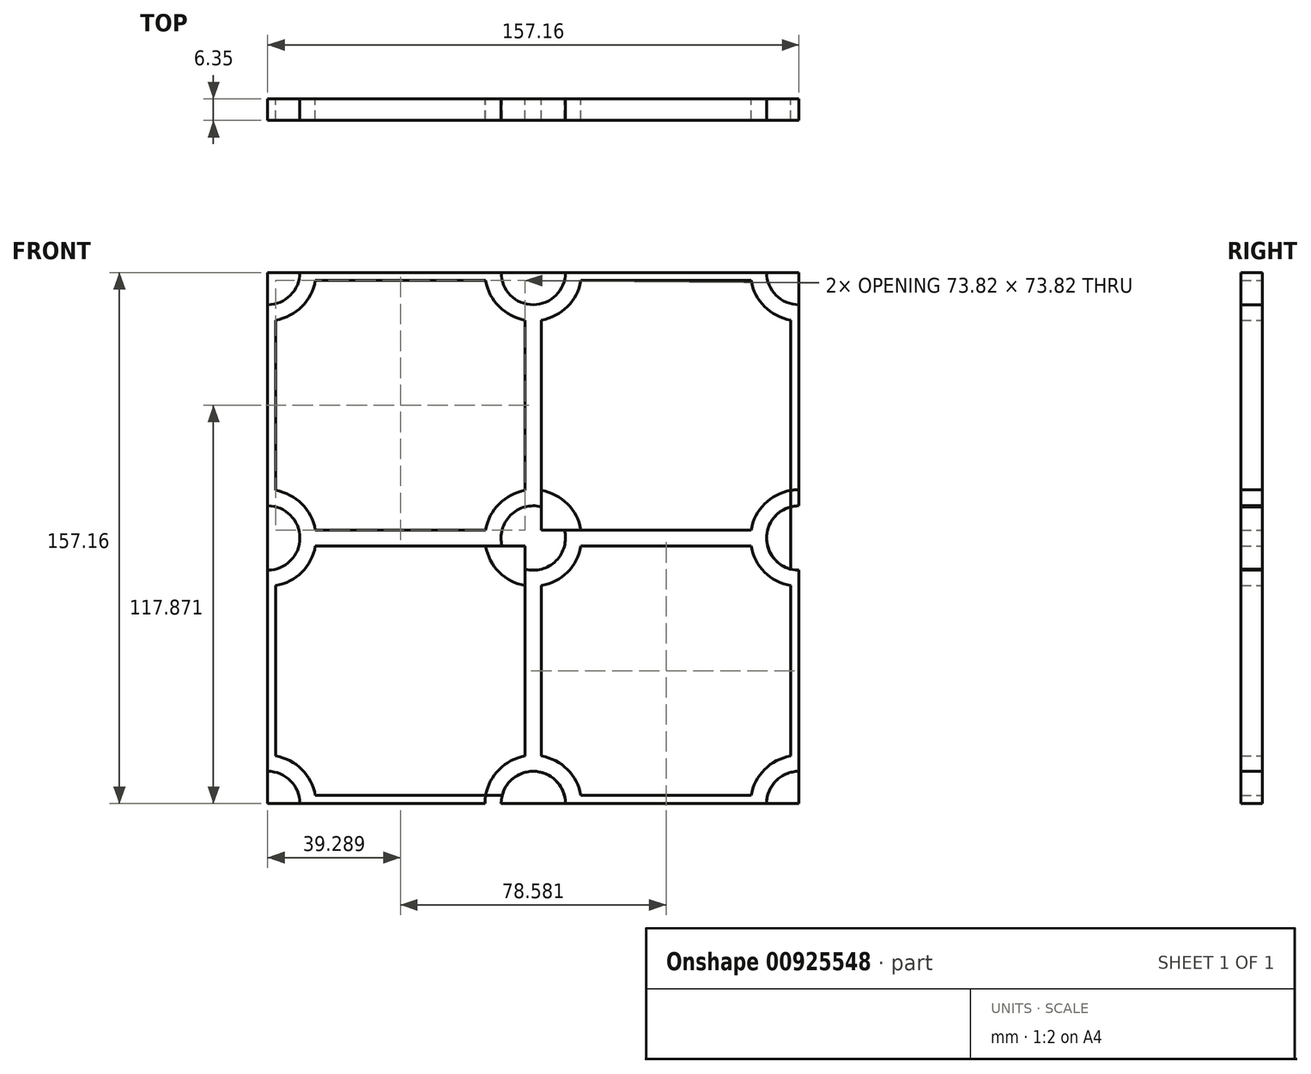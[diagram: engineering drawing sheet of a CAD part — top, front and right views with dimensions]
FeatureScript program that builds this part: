
annotation { "Feature Type Name" : "Feature", "Feature Type Description" : "" }
export const myFeature = defineFeature(function(context is Context, id is Id, definition is map)
    precondition{}
    {
        {
            var Q0;
            Q0=qCreatedBy(makeId("Front.planeOp"),FACE);
            var sketch = newSketch(context, id + "F0", { "sketchPlane" : qUnion([Q0])});
            skLineSegment(sketch, "E0.bottom", {"start": v(76.2, -76.2) * mm, "end": v(-76.2, -76.2) * mm});
            skLineSegment(sketch, "E0.top", {"start": v(76.2, 76.2) * mm, "end": v(-76.2, 76.2) * mm});
            skLineSegment(sketch, "E0.left", {"start": v(76.2, -76.2) * mm, "end": v(76.2, 76.2) * mm});
            skLineSegment(sketch, "E0.right", {"start": v(-76.2, -76.2) * mm, "end": v(-76.2, 76.2) * mm});
            skPoint(sketch, "E0.middle", {"position": v(0, 0) * mm});
            skSolve(sketch);
        }
        {
            var Q0;
            Q0=makeQuery(id+"F0.imprint","IMPRINT",FACE,{"disambiguationData":[TD([[makeQuery(id+"F0.imprint","IMPRINT",EDGE,{"derivedFrom":sQuery(id+"F0.wireOp",EDGE,"E0.bottom")}),-1.0]])]});
            var sketch = newSketch(context, id + "F1", { "sketchPlane" : qUnion([Q0])});
            skLineSegment(sketch, "E1.bottom", {"start": v(78.58, -78.58) * mm, "end": v(-78.58, -78.58) * mm});
            skLineSegment(sketch, "E1.top", {"start": v(78.58, 78.58) * mm, "end": v(-78.58, 78.58) * mm});
            skLineSegment(sketch, "E1.left", {"start": v(78.58, -78.58) * mm, "end": v(78.58, 78.58) * mm});
            skLineSegment(sketch, "E1.right", {"start": v(-78.58, -78.58) * mm, "end": v(-78.58, 78.58) * mm});
            skPoint(sketch, "E1.middle", {"position": v(0, 0) * mm});
            skLineSegment(sketch, "E2", {"start": v(-78.58, 0) * mm, "end": v(78.58, 0) * mm, "construction": true});
            skLineSegment(sketch, "E3", {"start": v(0, 78.58) * mm, "end": v(0, -78.58) * mm, "construction": true});
            skLineSegment(sketch, "E4.bottom", {"start": v(76.2, -76.2) * mm, "end": v(-76.2, -76.2) * mm});
            skLineSegment(sketch, "E4.top", {"start": v(76.2, 76.2) * mm, "end": v(-76.2, 76.2) * mm});
            skLineSegment(sketch, "E4.left", {"start": v(76.2, -76.2) * mm, "end": v(76.2, 76.2) * mm});
            skLineSegment(sketch, "E4.right", {"start": v(-76.2, -76.2) * mm, "end": v(-76.2, 76.2) * mm});
            skCircle(sketch, "E5", {"center": v(-78.58, 78.58) * mm, "radius": 9.53 * mm});
            skCircle(sketch, "E6", {"center": v(-78.58, 78.58) * mm, "radius": 14.29 * mm});
            skCircle(sketch, "E7.0.1.0", {"center": v(-78.58, 0) * mm, "radius": 14.29 * mm});
            skCircle(sketch, "E7.0.1.1", {"center": v(-78.58, 0) * mm, "radius": 9.53 * mm});
            skCircle(sketch, "E7.0.2.0", {"center": v(-78.58, -78.58) * mm, "radius": 14.29 * mm});
            skCircle(sketch, "E7.0.2.1", {"center": v(-78.58, -78.58) * mm, "radius": 9.53 * mm});
            skCircle(sketch, "E7.1.0.0", {"center": v(0, 78.58) * mm, "radius": 14.29 * mm});
            skCircle(sketch, "E7.1.0.1", {"center": v(0, 78.58) * mm, "radius": 9.53 * mm});
            skCircle(sketch, "E7.1.1.0", {"center": v(0, 0) * mm, "radius": 14.29 * mm});
            skCircle(sketch, "E7.1.1.1", {"center": v(0, 0) * mm, "radius": 9.53 * mm});
            skCircle(sketch, "E7.1.2.0", {"center": v(0, -78.58) * mm, "radius": 14.29 * mm});
            skCircle(sketch, "E7.1.2.1", {"center": v(0, -78.58) * mm, "radius": 9.53 * mm});
            skCircle(sketch, "E7.2.0.0", {"center": v(78.58, 78.58) * mm, "radius": 14.29 * mm});
            skCircle(sketch, "E7.2.0.1", {"center": v(78.58, 78.58) * mm, "radius": 9.53 * mm});
            skCircle(sketch, "E7.2.1.0", {"center": v(78.58, 0) * mm, "radius": 14.29 * mm});
            skCircle(sketch, "E7.2.1.1", {"center": v(78.58, 0) * mm, "radius": 9.53 * mm});
            skCircle(sketch, "E7.2.2.0", {"center": v(78.58, -78.58) * mm, "radius": 14.29 * mm});
            skCircle(sketch, "E7.2.2.1", {"center": v(78.58, -78.58) * mm, "radius": 9.53 * mm});
            skLineSegment(sketch, "E7.direction1", {"start": v(-78.58, 78.58) * mm, "end": v(0, 78.58) * mm, "construction": true});
            skLineSegment(sketch, "E7.direction2", {"start": v(-78.58, 78.58) * mm, "end": v(-78.58, 0) * mm, "construction": true});
            skLineSegment(sketch, "E8.0", {"start": v(-2.38, 76.2) * mm, "end": v(-2.38, -76.2) * mm});
            skLineSegment(sketch, "E9.0", {"start": v(2.38, 76.2) * mm, "end": v(2.38, -76.2) * mm});
            skLineSegment(sketch, "E10.0", {"start": v(-76.2, -2.38) * mm, "end": v(76.2, -2.38) * mm});
            skLineSegment(sketch, "E11.0", {"start": v(-76.2, 2.38) * mm, "end": v(76.2, 2.38) * mm});
            skSolve(sketch);
        }
        {
            var Q0;
            {var subQ7=sQuery(id+"F1.wireOp",EDGE,"E7.1.0.0");var subQ8=sQuery(id+"F1.wireOp",EDGE,"E4.top");var subQ9=makeQuery(id+"F1.imprint","INTERSECT",VERTEX,{"disambiguationData":[OD(1.0)],"derivedFrom":[subQ8,subQ7]});Q0=makeQuery(id+"F1.imprint","IMPRINT",FACE,{"disambiguationData":[TD([[makeQuery(id+"F1.imprint","IMPRINT",EDGE,{"disambiguationData":[TD([[subQ9,-1.0]])],"derivedFrom":subQ8}),1.0]])]});}
            var Q1;
            {var subQ6=sQuery(id+"F1.wireOp",EDGE,"E4.top");var subQ12=sQuery(id+"F1.wireOp",EDGE,"E7.2.0.0");var subQ14=makeQuery(id+"F1.imprint","INTERSECT",VERTEX,{"derivedFrom":[subQ6,subQ12]});Q1=makeQuery(id+"F1.imprint","IMPRINT",FACE,{"disambiguationData":[TD([[makeQuery(id+"F1.imprint","IMPRINT",EDGE,{"disambiguationData":[TD([[subQ14,-1.0]])],"derivedFrom":subQ6}),1.0]])]});}
            var Q2;
            {var subQ6=sQuery(id+"F1.wireOp",EDGE,"E4.bottom");var subQ9=sQuery(id+"F1.wireOp",EDGE,"E7.1.2.0");var subQ10=makeQuery(id+"F1.imprint","INTERSECT",VERTEX,{"disambiguationData":[OD(1.0)],"derivedFrom":[subQ6,subQ9]});Q2=makeQuery(id+"F1.imprint","IMPRINT",FACE,{"disambiguationData":[TD([[makeQuery(id+"F1.imprint","IMPRINT",EDGE,{"disambiguationData":[TD([[subQ10,-1.0]])],"derivedFrom":subQ6}),-1.0]])]});}
            var Q3;
            {var subQ1=sQuery(id+"F1.wireOp",EDGE,"E4.bottom");var subQ9=sQuery(id+"F1.wireOp",EDGE,"E7.2.2.0");var subQ14=makeQuery(id+"F1.imprint","INTERSECT",VERTEX,{"derivedFrom":[subQ1,subQ9]});Q3=makeQuery(id+"F1.imprint","IMPRINT",FACE,{"disambiguationData":[TD([[makeQuery(id+"F1.imprint","IMPRINT",EDGE,{"disambiguationData":[TD([[subQ14,-1.0]])],"derivedFrom":subQ1}),-1.0]])]});}
            extrude(context, id + "F2", {"entities" : qUnion([Q0, Q1, Q2, Q3]), "depth" : 6.35 * mm, "offsetDistance" : 30.48 * mm});
        }
        {
            var Q0;
            {var subQ0=sQuery(id+"F1.wireOp",EDGE,"E4.right");var subQ1=sQuery(id+"F1.wireOp",EDGE,"E4.top");var subQ2=makeQuery(id+"F1.imprint","INTERSECT",VERTEX,{"derivedFrom":[subQ1,subQ0]});Q0=makeQuery(id+"F1.imprint","IMPRINT",FACE,{"disambiguationData":[TD([[makeQuery(id+"F1.imprint","IMPRINT",EDGE,{"disambiguationData":[TD([[subQ2,1.0]])],"derivedFrom":subQ1}),1.0]])]});}
            var Q1;
            {var subQ5=sQuery(id+"F1.wireOp",EDGE,"E1.right");var subQ6=sQuery(id+"F1.wireOp",EDGE,"E1.top");var subQ7=makeQuery(id+"F1.imprint","INTERSECT",VERTEX,{"derivedFrom":[subQ6,subQ5]});Q1=makeQuery(id+"F1.imprint","IMPRINT",FACE,{"disambiguationData":[TD([[makeQuery(id+"F1.imprint","IMPRINT",EDGE,{"disambiguationData":[TD([[subQ7,1.0]])],"derivedFrom":subQ6}),1.0]])]});}
            var Q2;
            {var subQ3=sQuery(id+"F1.wireOp",EDGE,"E7.1.0.1");var subQ6=sQuery(id+"F1.wireOp",EDGE,"E1.top");var subQ7=makeQuery(id+"F1.imprint","INTERSECT",VERTEX,{"disambiguationData":[OD(0.0)],"derivedFrom":[subQ6,subQ3]});Q2=makeQuery(id+"F1.imprint","IMPRINT",FACE,{"disambiguationData":[TD([[makeQuery(id+"F1.imprint","IMPRINT",EDGE,{"disambiguationData":[TD([[subQ7,-1.0]])],"derivedFrom":subQ6}),1.0]])]});}
            var Q3;
            {var subQ0=sQuery(id+"F1.wireOp",EDGE,"E8.0");var subQ1=sQuery(id+"F1.wireOp",EDGE,"E4.top");var subQ2=makeQuery(id+"F1.imprint","INTERSECT",VERTEX,{"derivedFrom":[subQ1,subQ0]});Q3=makeQuery(id+"F1.imprint","IMPRINT",FACE,{"disambiguationData":[TD([[makeQuery(id+"F1.imprint","IMPRINT",EDGE,{"disambiguationData":[TD([[subQ2,-1.0]])],"derivedFrom":subQ1}),1.0]])]});}
            var Q4;
            {var subQ0=sQuery(id+"F1.wireOp",EDGE,"E8.0");var subQ1=sQuery(id+"F1.wireOp",EDGE,"E4.top");var subQ2=makeQuery(id+"F1.imprint","INTERSECT",VERTEX,{"derivedFrom":[subQ1,subQ0]});Q4=makeQuery(id+"F1.imprint","IMPRINT",FACE,{"disambiguationData":[TD([[makeQuery(id+"F1.imprint","IMPRINT",EDGE,{"disambiguationData":[TD([[subQ2,1.0]])],"derivedFrom":subQ1}),1.0]])]});}
            var Q5;
            {var subQ0=sQuery(id+"F1.wireOp",EDGE,"E9.0");var subQ1=sQuery(id+"F1.wireOp",EDGE,"E4.top");var subQ2=makeQuery(id+"F1.imprint","INTERSECT",VERTEX,{"derivedFrom":[subQ1,subQ0]});Q5=makeQuery(id+"F1.imprint","IMPRINT",FACE,{"disambiguationData":[TD([[makeQuery(id+"F1.imprint","IMPRINT",EDGE,{"disambiguationData":[TD([[subQ2,1.0]])],"derivedFrom":subQ1}),1.0]])]});}
            var Q6;
            {var subQ0=sQuery(id+"F1.wireOp",EDGE,"E4.left");var subQ1=sQuery(id+"F1.wireOp",EDGE,"E4.top");var subQ2=makeQuery(id+"F1.imprint","INTERSECT",VERTEX,{"derivedFrom":[subQ1,subQ0]});Q6=makeQuery(id+"F1.imprint","IMPRINT",FACE,{"disambiguationData":[TD([[makeQuery(id+"F1.imprint","IMPRINT",EDGE,{"disambiguationData":[TD([[subQ2,-1.0]])],"derivedFrom":subQ1}),1.0]])]});}
            var Q7;
            {var subQ6=sQuery(id+"F1.wireOp",EDGE,"E1.left");var subQ7=sQuery(id+"F1.wireOp",EDGE,"E1.top");var subQ8=makeQuery(id+"F1.imprint","INTERSECT",VERTEX,{"derivedFrom":[subQ7,subQ6]});Q7=makeQuery(id+"F1.imprint","IMPRINT",FACE,{"disambiguationData":[TD([[makeQuery(id+"F1.imprint","IMPRINT",EDGE,{"disambiguationData":[TD([[subQ8,-1.0]])],"derivedFrom":subQ7}),1.0]])]});}
            var Q8;
            {var subQ0=sQuery(id+"F1.wireOp",EDGE,"E11.0");var subQ1=sQuery(id+"F1.wireOp",EDGE,"E4.left");var subQ2=makeQuery(id+"F1.imprint","INTERSECT",VERTEX,{"derivedFrom":[subQ1,subQ0]});Q8=makeQuery(id+"F1.imprint","IMPRINT",FACE,{"disambiguationData":[TD([[makeQuery(id+"F1.imprint","IMPRINT",EDGE,{"disambiguationData":[TD([[subQ2,-1.0]])],"derivedFrom":subQ1}),1.0]])]});}
            var Q9;
            {var subQ2=sQuery(id+"F1.wireOp",EDGE,"E7.2.1.1");var subQ5=sQuery(id+"F1.wireOp",EDGE,"E1.left");var subQ8=makeQuery(id+"F1.imprint","INTERSECT",VERTEX,{"disambiguationData":[OD(0.0)],"derivedFrom":[subQ5,subQ2]});Q9=makeQuery(id+"F1.imprint","IMPRINT",FACE,{"disambiguationData":[TD([[makeQuery(id+"F1.imprint","IMPRINT",EDGE,{"disambiguationData":[TD([[subQ8,-1.0]])],"derivedFrom":subQ5}),1.0]])]});}
            var Q10;
            {var subQ0=sQuery(id+"F1.wireOp",EDGE,"E10.0");var subQ1=sQuery(id+"F1.wireOp",EDGE,"E4.left");var subQ2=makeQuery(id+"F1.imprint","INTERSECT",VERTEX,{"derivedFrom":[subQ1,subQ0]});Q10=makeQuery(id+"F1.imprint","IMPRINT",FACE,{"disambiguationData":[TD([[makeQuery(id+"F1.imprint","IMPRINT",EDGE,{"disambiguationData":[TD([[subQ2,-1.0]])],"derivedFrom":subQ1}),1.0]])]});}
            var Q11;
            {var subQ0=sQuery(id+"F1.wireOp",EDGE,"E10.0");var subQ1=sQuery(id+"F1.wireOp",EDGE,"E4.left");var subQ2=makeQuery(id+"F1.imprint","INTERSECT",VERTEX,{"derivedFrom":[subQ1,subQ0]});Q11=makeQuery(id+"F1.imprint","IMPRINT",FACE,{"disambiguationData":[TD([[makeQuery(id+"F1.imprint","IMPRINT",EDGE,{"disambiguationData":[TD([[subQ2,1.0]])],"derivedFrom":subQ1}),1.0]])]});}
            var Q12;
            {var subQ0=sQuery(id+"F1.wireOp",EDGE,"E4.left");var subQ1=sQuery(id+"F1.wireOp",EDGE,"E4.bottom");var subQ2=makeQuery(id+"F1.imprint","INTERSECT",VERTEX,{"derivedFrom":[subQ1,subQ0]});Q12=makeQuery(id+"F1.imprint","IMPRINT",FACE,{"disambiguationData":[TD([[makeQuery(id+"F1.imprint","IMPRINT",EDGE,{"disambiguationData":[TD([[subQ2,-1.0]])],"derivedFrom":subQ1}),-1.0]])]});}
            var Q13;
            {var subQ6=sQuery(id+"F1.wireOp",EDGE,"E1.left");var subQ7=sQuery(id+"F1.wireOp",EDGE,"E1.bottom");var subQ8=makeQuery(id+"F1.imprint","INTERSECT",VERTEX,{"derivedFrom":[subQ7,subQ6]});Q13=makeQuery(id+"F1.imprint","IMPRINT",FACE,{"disambiguationData":[TD([[makeQuery(id+"F1.imprint","IMPRINT",EDGE,{"disambiguationData":[TD([[subQ8,-1.0]])],"derivedFrom":subQ7}),-1.0]])]});}
            var Q14;
            {var subQ0=sQuery(id+"F1.wireOp",EDGE,"E9.0");var subQ1=sQuery(id+"F1.wireOp",EDGE,"E4.bottom");var subQ2=makeQuery(id+"F1.imprint","INTERSECT",VERTEX,{"derivedFrom":[subQ1,subQ0]});Q14=makeQuery(id+"F1.imprint","IMPRINT",FACE,{"disambiguationData":[TD([[makeQuery(id+"F1.imprint","IMPRINT",EDGE,{"disambiguationData":[TD([[subQ2,1.0]])],"derivedFrom":subQ1}),-1.0]])]});}
            var Q15;
            {var subQ0=sQuery(id+"F1.wireOp",EDGE,"E8.0");var subQ1=sQuery(id+"F1.wireOp",EDGE,"E4.bottom");var subQ2=makeQuery(id+"F1.imprint","INTERSECT",VERTEX,{"derivedFrom":[subQ1,subQ0]});Q15=makeQuery(id+"F1.imprint","IMPRINT",FACE,{"disambiguationData":[TD([[makeQuery(id+"F1.imprint","IMPRINT",EDGE,{"disambiguationData":[TD([[subQ2,-1.0]])],"derivedFrom":subQ1}),-1.0]])]});}
            var Q16;
            {var subQ2=sQuery(id+"F1.wireOp",EDGE,"E7.1.2.1");var subQ6=sQuery(id+"F1.wireOp",EDGE,"E1.bottom");var subQ7=makeQuery(id+"F1.imprint","INTERSECT",VERTEX,{"disambiguationData":[OD(0.0)],"derivedFrom":[subQ6,subQ2]});Q16=makeQuery(id+"F1.imprint","IMPRINT",FACE,{"disambiguationData":[TD([[makeQuery(id+"F1.imprint","IMPRINT",EDGE,{"disambiguationData":[TD([[subQ7,-1.0]])],"derivedFrom":subQ6}),-1.0]])]});}
            var Q17;
            {var subQ0=sQuery(id+"F1.wireOp",EDGE,"E8.0");var subQ1=sQuery(id+"F1.wireOp",EDGE,"E4.bottom");var subQ2=makeQuery(id+"F1.imprint","INTERSECT",VERTEX,{"derivedFrom":[subQ1,subQ0]});Q17=makeQuery(id+"F1.imprint","IMPRINT",FACE,{"disambiguationData":[TD([[makeQuery(id+"F1.imprint","IMPRINT",EDGE,{"disambiguationData":[TD([[subQ2,1.0]])],"derivedFrom":subQ1}),-1.0]])]});}
            var Q18;
            {var subQ0=sQuery(id+"F1.wireOp",EDGE,"E9.0");var subQ1=sQuery(id+"F1.wireOp",EDGE,"E7.1.1.1");var subQ2=makeQuery(id+"F1.imprint","INTERSECT",VERTEX,{"disambiguationData":[OD(1.0)],"derivedFrom":[subQ1,subQ0]});Q18=makeQuery(id+"F1.imprint","IMPRINT",FACE,{"disambiguationData":[TD([[makeQuery(id+"F1.imprint","IMPRINT",EDGE,{"disambiguationData":[TD([[subQ2,-1.0]])],"derivedFrom":subQ1}),1.0]])]});}
            var Q19;
            {var subQ0=sQuery(id+"F1.wireOp",EDGE,"E8.0");var subQ1=sQuery(id+"F1.wireOp",EDGE,"E7.1.1.1");var subQ2=makeQuery(id+"F1.imprint","INTERSECT",VERTEX,{"disambiguationData":[OD(1.0)],"derivedFrom":[subQ1,subQ0]});Q19=makeQuery(id+"F1.imprint","IMPRINT",FACE,{"disambiguationData":[TD([[makeQuery(id+"F1.imprint","IMPRINT",EDGE,{"disambiguationData":[TD([[subQ2,-1.0]])],"derivedFrom":subQ1}),1.0]])]});}
            var Q20;
            {var subQ0=sQuery(id+"F1.wireOp",EDGE,"E10.0");var subQ1=sQuery(id+"F1.wireOp",EDGE,"E7.1.1.1");var subQ2=makeQuery(id+"F1.imprint","INTERSECT",VERTEX,{"disambiguationData":[OD(0.0)],"derivedFrom":[subQ1,subQ0]});Q20=makeQuery(id+"F1.imprint","IMPRINT",FACE,{"disambiguationData":[TD([[makeQuery(id+"F1.imprint","IMPRINT",EDGE,{"disambiguationData":[TD([[subQ2,-1.0]])],"derivedFrom":subQ1}),1.0]])]});}
            var Q21;
            {var subQ0=sQuery(id+"F1.wireOp",EDGE,"E11.0");var subQ1=sQuery(id+"F1.wireOp",EDGE,"E7.1.1.1");var subQ2=makeQuery(id+"F1.imprint","INTERSECT",VERTEX,{"disambiguationData":[OD(1.0)],"derivedFrom":[subQ1,subQ0]});Q21=makeQuery(id+"F1.imprint","IMPRINT",FACE,{"disambiguationData":[TD([[makeQuery(id+"F1.imprint","IMPRINT",EDGE,{"disambiguationData":[TD([[subQ2,-1.0]])],"derivedFrom":subQ1}),1.0]])]});}
            var Q22;
            {var subQ0=sQuery(id+"F1.wireOp",EDGE,"E8.0");var subQ1=sQuery(id+"F1.wireOp",EDGE,"E7.1.1.1");var subQ2=makeQuery(id+"F1.imprint","INTERSECT",VERTEX,{"disambiguationData":[OD(0.0)],"derivedFrom":[subQ1,subQ0]});Q22=makeQuery(id+"F1.imprint","IMPRINT",FACE,{"disambiguationData":[TD([[makeQuery(id+"F1.imprint","IMPRINT",EDGE,{"disambiguationData":[TD([[subQ2,-1.0]])],"derivedFrom":subQ1}),1.0]])]});}
            var Q23;
            {var subQ0=sQuery(id+"F1.wireOp",EDGE,"E9.0");var subQ1=sQuery(id+"F1.wireOp",EDGE,"E7.1.1.1");var subQ2=makeQuery(id+"F1.imprint","INTERSECT",VERTEX,{"disambiguationData":[OD(0.0)],"derivedFrom":[subQ1,subQ0]});Q23=makeQuery(id+"F1.imprint","IMPRINT",FACE,{"disambiguationData":[TD([[makeQuery(id+"F1.imprint","IMPRINT",EDGE,{"disambiguationData":[TD([[subQ2,-1.0]])],"derivedFrom":subQ1}),1.0]])]});}
            var Q24;
            {var subQ0=sQuery(id+"F1.wireOp",EDGE,"E9.0");var subQ1=sQuery(id+"F1.wireOp",EDGE,"E7.1.1.1");var subQ2=makeQuery(id+"F1.imprint","INTERSECT",VERTEX,{"disambiguationData":[OD(0.0)],"derivedFrom":[subQ1,subQ0]});Q24=makeQuery(id+"F1.imprint","IMPRINT",FACE,{"disambiguationData":[TD([[makeQuery(id+"F1.imprint","IMPRINT",EDGE,{"disambiguationData":[TD([[subQ2,1.0]])],"derivedFrom":subQ1}),1.0]])]});}
            var Q25;
            {var subQ0=sQuery(id+"F1.wireOp",EDGE,"E11.0");var subQ1=sQuery(id+"F1.wireOp",EDGE,"E7.1.1.1");var subQ2=makeQuery(id+"F1.imprint","INTERSECT",VERTEX,{"disambiguationData":[OD(0.0)],"derivedFrom":[subQ1,subQ0]});Q25=makeQuery(id+"F1.imprint","IMPRINT",FACE,{"disambiguationData":[TD([[makeQuery(id+"F1.imprint","IMPRINT",EDGE,{"disambiguationData":[TD([[subQ2,1.0]])],"derivedFrom":subQ1}),1.0]])]});}
            var Q26;
            {var subQ0=sQuery(id+"F1.wireOp",EDGE,"E11.0");var subQ1=sQuery(id+"F1.wireOp",EDGE,"E8.0");var subQ2=makeQuery(id+"F1.imprint","INTERSECT",VERTEX,{"derivedFrom":[subQ1,subQ0]});Q26=makeQuery(id+"F1.imprint","IMPRINT",FACE,{"disambiguationData":[TD([[makeQuery(id+"F1.imprint","IMPRINT",EDGE,{"disambiguationData":[TD([[subQ2,-1.0]])],"derivedFrom":subQ1}),1.0]])]});}
            var Q27;
            {var subQ0=sQuery(id+"F1.wireOp",EDGE,"E4.right");var subQ1=sQuery(id+"F1.wireOp",EDGE,"E4.bottom");var subQ2=makeQuery(id+"F1.imprint","INTERSECT",VERTEX,{"derivedFrom":[subQ1,subQ0]});Q27=makeQuery(id+"F1.imprint","IMPRINT",FACE,{"disambiguationData":[TD([[makeQuery(id+"F1.imprint","IMPRINT",EDGE,{"disambiguationData":[TD([[subQ2,1.0]])],"derivedFrom":subQ1}),-1.0]])]});}
            var Q28;
            {var subQ6=sQuery(id+"F1.wireOp",EDGE,"E1.right");var subQ7=sQuery(id+"F1.wireOp",EDGE,"E1.bottom");var subQ8=makeQuery(id+"F1.imprint","INTERSECT",VERTEX,{"derivedFrom":[subQ7,subQ6]});Q28=makeQuery(id+"F1.imprint","IMPRINT",FACE,{"disambiguationData":[TD([[makeQuery(id+"F1.imprint","IMPRINT",EDGE,{"disambiguationData":[TD([[subQ8,1.0]])],"derivedFrom":subQ7}),-1.0]])]});}
            var Q29;
            {var subQ0=sQuery(id+"F1.wireOp",EDGE,"E10.0");var subQ1=sQuery(id+"F1.wireOp",EDGE,"E4.right");var subQ2=makeQuery(id+"F1.imprint","INTERSECT",VERTEX,{"derivedFrom":[subQ1,subQ0]});Q29=makeQuery(id+"F1.imprint","IMPRINT",FACE,{"disambiguationData":[TD([[makeQuery(id+"F1.imprint","IMPRINT",EDGE,{"disambiguationData":[TD([[subQ2,1.0]])],"derivedFrom":subQ1}),-1.0]])]});}
            var Q30;
            {var subQ2=sQuery(id+"F1.wireOp",EDGE,"E7.0.1.1");var subQ4=sQuery(id+"F1.wireOp",EDGE,"E1.right");var subQ5=makeQuery(id+"F1.imprint","INTERSECT",VERTEX,{"disambiguationData":[OD(0.0)],"derivedFrom":[subQ4,subQ2]});Q30=makeQuery(id+"F1.imprint","IMPRINT",FACE,{"disambiguationData":[TD([[makeQuery(id+"F1.imprint","IMPRINT",EDGE,{"disambiguationData":[TD([[subQ5,-1.0]])],"derivedFrom":subQ4}),-1.0]])]});}
            var Q31;
            {var subQ0=sQuery(id+"F1.wireOp",EDGE,"E10.0");var subQ1=sQuery(id+"F1.wireOp",EDGE,"E4.right");var subQ2=makeQuery(id+"F1.imprint","INTERSECT",VERTEX,{"derivedFrom":[subQ1,subQ0]});Q31=makeQuery(id+"F1.imprint","IMPRINT",FACE,{"disambiguationData":[TD([[makeQuery(id+"F1.imprint","IMPRINT",EDGE,{"disambiguationData":[TD([[subQ2,-1.0]])],"derivedFrom":subQ1}),-1.0]])]});}
            var Q32;
            {var subQ0=sQuery(id+"F1.wireOp",EDGE,"E11.0");var subQ1=sQuery(id+"F1.wireOp",EDGE,"E4.right");var subQ2=makeQuery(id+"F1.imprint","INTERSECT",VERTEX,{"derivedFrom":[subQ1,subQ0]});Q32=makeQuery(id+"F1.imprint","IMPRINT",FACE,{"disambiguationData":[TD([[makeQuery(id+"F1.imprint","IMPRINT",EDGE,{"disambiguationData":[TD([[subQ2,-1.0]])],"derivedFrom":subQ1}),-1.0]])]});}
            extrude(context, id + "F3", {"entities" : qUnion([Q0, Q1, Q2, Q3, Q4, Q5, Q6, Q7, Q8, Q9, Q10, Q11, Q12, Q13, Q14, Q15, Q16, Q17, Q18, Q19, Q20, Q21, Q22, Q23, Q24, Q25, Q26, Q27, Q28, Q29, Q30, Q31, Q32]), "depth" : 6.35 * mm, "offsetDistance" : 30.48 * mm});
        }
        {
            var Q0;
            {var subQ0=sQuery(id+"F1.wireOp",EDGE,"E6");var subQ1=sQuery(id+"F1.wireOp",EDGE,"E1.top");var subQ2=makeQuery(id+"F1.imprint","INTERSECT",VERTEX,{"derivedFrom":[subQ1,subQ0]});Q0=makeQuery(id+"F1.imprint","IMPRINT",FACE,{"disambiguationData":[TD([[makeQuery(id+"F1.imprint","IMPRINT",EDGE,{"disambiguationData":[TD([[subQ2,-1.0]])],"derivedFrom":subQ1}),1.0]])]});}
            var Q1;
            {var subQ0=sQuery(id+"F1.wireOp",EDGE,"E6");var subQ1=sQuery(id+"F1.wireOp",EDGE,"E4.top");var subQ2=makeQuery(id+"F1.imprint","INTERSECT",VERTEX,{"derivedFrom":[subQ1,subQ0]});Q1=makeQuery(id+"F1.imprint","IMPRINT",FACE,{"disambiguationData":[TD([[makeQuery(id+"F1.imprint","IMPRINT",EDGE,{"disambiguationData":[TD([[subQ2,-1.0]])],"derivedFrom":subQ1}),1.0]])]});}
            var Q2;
            {var subQ0=sQuery(id+"F1.wireOp",EDGE,"E6");var subQ1=sQuery(id+"F1.wireOp",EDGE,"E1.right");var subQ2=makeQuery(id+"F1.imprint","INTERSECT",VERTEX,{"derivedFrom":[subQ1,subQ0]});Q2=makeQuery(id+"F1.imprint","IMPRINT",FACE,{"disambiguationData":[TD([[makeQuery(id+"F1.imprint","IMPRINT",EDGE,{"disambiguationData":[TD([[subQ2,-1.0]])],"derivedFrom":subQ1}),-1.0]])]});}
            var Q3;
            {var subQ0=sQuery(id+"F1.wireOp",EDGE,"E7.0.1.0");var subQ1=sQuery(id+"F1.wireOp",EDGE,"E1.right");var subQ2=makeQuery(id+"F1.imprint","INTERSECT",VERTEX,{"disambiguationData":[OD(1.0)],"derivedFrom":[subQ1,subQ0]});Q3=makeQuery(id+"F1.imprint","IMPRINT",FACE,{"disambiguationData":[TD([[makeQuery(id+"F1.imprint","IMPRINT",EDGE,{"disambiguationData":[TD([[subQ2,-1.0]])],"derivedFrom":subQ1}),-1.0]])]});}
            var Q4;
            {var subQ0=sQuery(id+"F1.wireOp",EDGE,"E7.0.1.0");var subQ1=sQuery(id+"F1.wireOp",EDGE,"E1.right");var subQ2=makeQuery(id+"F1.imprint","INTERSECT",VERTEX,{"disambiguationData":[OD(1.0)],"derivedFrom":[subQ1,subQ0]});Q4=makeQuery(id+"F1.imprint","IMPRINT",FACE,{"disambiguationData":[TD([[makeQuery(id+"F1.imprint","IMPRINT",EDGE,{"disambiguationData":[TD([[subQ2,1.0]])],"derivedFrom":subQ1}),-1.0]])]});}
            var Q5;
            {var subQ0=sQuery(id+"F1.wireOp",EDGE,"E7.0.1.1");var subQ1=sQuery(id+"F1.wireOp",EDGE,"E4.right");var subQ2=makeQuery(id+"F1.imprint","INTERSECT",VERTEX,{"disambiguationData":[OD(1.0)],"derivedFrom":[subQ1,subQ0]});Q5=makeQuery(id+"F1.imprint","IMPRINT",FACE,{"disambiguationData":[TD([[makeQuery(id+"F1.imprint","IMPRINT",EDGE,{"disambiguationData":[TD([[subQ2,-1.0]])],"derivedFrom":subQ1}),-1.0]])]});}
            var Q6;
            {var subQ0=sQuery(id+"F1.wireOp",EDGE,"E11.0");var subQ1=sQuery(id+"F1.wireOp",EDGE,"E7.0.1.0");var subQ2=makeQuery(id+"F1.imprint","INTERSECT",VERTEX,{"derivedFrom":[subQ1,subQ0]});Q6=makeQuery(id+"F1.imprint","IMPRINT",FACE,{"disambiguationData":[TD([[makeQuery(id+"F1.imprint","IMPRINT",EDGE,{"disambiguationData":[TD([[subQ2,1.0]])],"derivedFrom":subQ1}),1.0]])]});}
            var Q7;
            {var subQ0=sQuery(id+"F1.wireOp",EDGE,"E7.0.1.0");var subQ1=sQuery(id+"F1.wireOp",EDGE,"E4.right");var subQ2=makeQuery(id+"F1.imprint","INTERSECT",VERTEX,{"disambiguationData":[OD(0.0)],"derivedFrom":[subQ1,subQ0]});Q7=makeQuery(id+"F1.imprint","IMPRINT",FACE,{"disambiguationData":[TD([[makeQuery(id+"F1.imprint","IMPRINT",EDGE,{"disambiguationData":[TD([[subQ2,-1.0]])],"derivedFrom":subQ1}),-1.0]])]});}
            var Q8;
            {var subQ0=sQuery(id+"F1.wireOp",EDGE,"E11.0");var subQ1=sQuery(id+"F1.wireOp",EDGE,"E7.0.1.0");var subQ2=makeQuery(id+"F1.imprint","INTERSECT",VERTEX,{"derivedFrom":[subQ1,subQ0]});Q8=makeQuery(id+"F1.imprint","IMPRINT",FACE,{"disambiguationData":[TD([[makeQuery(id+"F1.imprint","IMPRINT",EDGE,{"disambiguationData":[TD([[subQ2,1.0]])],"derivedFrom":subQ1}),-1.0]])]});}
            var Q9;
            {var subQ0=sQuery(id+"F1.wireOp",EDGE,"E8.0");var subQ1=sQuery(id+"F1.wireOp",EDGE,"E7.1.1.0");var subQ2=makeQuery(id+"F1.imprint","INTERSECT",VERTEX,{"disambiguationData":[OD(0.0)],"derivedFrom":[subQ1,subQ0]});Q9=makeQuery(id+"F1.imprint","IMPRINT",FACE,{"disambiguationData":[TD([[makeQuery(id+"F1.imprint","IMPRINT",EDGE,{"disambiguationData":[TD([[subQ2,-1.0]])],"derivedFrom":subQ1}),1.0]])]});}
            var Q10;
            {var subQ0=sQuery(id+"F1.wireOp",EDGE,"E11.0");var subQ1=sQuery(id+"F1.wireOp",EDGE,"E7.1.1.0");var subQ2=makeQuery(id+"F1.imprint","INTERSECT",VERTEX,{"disambiguationData":[OD(1.0)],"derivedFrom":[subQ1,subQ0]});Q10=makeQuery(id+"F1.imprint","IMPRINT",FACE,{"disambiguationData":[TD([[makeQuery(id+"F1.imprint","IMPRINT",EDGE,{"disambiguationData":[TD([[subQ2,-1.0]])],"derivedFrom":subQ1}),1.0]])]});}
            var Q11;
            {var subQ0=sQuery(id+"F1.wireOp",EDGE,"E10.0");var subQ1=sQuery(id+"F1.wireOp",EDGE,"E7.1.1.0");var subQ2=makeQuery(id+"F1.imprint","INTERSECT",VERTEX,{"disambiguationData":[OD(0.0)],"derivedFrom":[subQ1,subQ0]});Q11=makeQuery(id+"F1.imprint","IMPRINT",FACE,{"disambiguationData":[TD([[makeQuery(id+"F1.imprint","IMPRINT",EDGE,{"disambiguationData":[TD([[subQ2,-1.0]])],"derivedFrom":subQ1}),1.0]])]});}
            var Q12;
            {var subQ0=sQuery(id+"F1.wireOp",EDGE,"E8.0");var subQ1=sQuery(id+"F1.wireOp",EDGE,"E7.1.1.0");var subQ2=makeQuery(id+"F1.imprint","INTERSECT",VERTEX,{"disambiguationData":[OD(1.0)],"derivedFrom":[subQ1,subQ0]});Q12=makeQuery(id+"F1.imprint","IMPRINT",FACE,{"disambiguationData":[TD([[makeQuery(id+"F1.imprint","IMPRINT",EDGE,{"disambiguationData":[TD([[subQ2,-1.0]])],"derivedFrom":subQ1}),1.0]])]});}
            var Q13;
            {var subQ0=sQuery(id+"F1.wireOp",EDGE,"E9.0");var subQ1=sQuery(id+"F1.wireOp",EDGE,"E7.1.1.0");var subQ2=makeQuery(id+"F1.imprint","INTERSECT",VERTEX,{"disambiguationData":[OD(1.0)],"derivedFrom":[subQ1,subQ0]});Q13=makeQuery(id+"F1.imprint","IMPRINT",FACE,{"disambiguationData":[TD([[makeQuery(id+"F1.imprint","IMPRINT",EDGE,{"disambiguationData":[TD([[subQ2,-1.0]])],"derivedFrom":subQ1}),1.0]])]});}
            var Q14;
            {var subQ0=sQuery(id+"F1.wireOp",EDGE,"E9.0");var subQ1=sQuery(id+"F1.wireOp",EDGE,"E7.1.1.0");var subQ2=makeQuery(id+"F1.imprint","INTERSECT",VERTEX,{"disambiguationData":[OD(0.0)],"derivedFrom":[subQ1,subQ0]});Q14=makeQuery(id+"F1.imprint","IMPRINT",FACE,{"disambiguationData":[TD([[makeQuery(id+"F1.imprint","IMPRINT",EDGE,{"disambiguationData":[TD([[subQ2,1.0]])],"derivedFrom":subQ1}),1.0]])]});}
            var Q15;
            {var subQ0=sQuery(id+"F1.wireOp",EDGE,"E11.0");var subQ1=sQuery(id+"F1.wireOp",EDGE,"E7.1.1.0");var subQ2=makeQuery(id+"F1.imprint","INTERSECT",VERTEX,{"disambiguationData":[OD(0.0)],"derivedFrom":[subQ1,subQ0]});Q15=makeQuery(id+"F1.imprint","IMPRINT",FACE,{"disambiguationData":[TD([[makeQuery(id+"F1.imprint","IMPRINT",EDGE,{"disambiguationData":[TD([[subQ2,1.0]])],"derivedFrom":subQ1}),1.0]])]});}
            var Q16;
            {var subQ0=sQuery(id+"F1.wireOp",EDGE,"E9.0");var subQ1=sQuery(id+"F1.wireOp",EDGE,"E7.1.1.0");var subQ2=makeQuery(id+"F1.imprint","INTERSECT",VERTEX,{"disambiguationData":[OD(0.0)],"derivedFrom":[subQ1,subQ0]});Q16=makeQuery(id+"F1.imprint","IMPRINT",FACE,{"disambiguationData":[TD([[makeQuery(id+"F1.imprint","IMPRINT",EDGE,{"disambiguationData":[TD([[subQ2,-1.0]])],"derivedFrom":subQ1}),1.0]])]});}
            var Q17;
            {var subQ0=sQuery(id+"F1.wireOp",EDGE,"E8.0");var subQ1=sQuery(id+"F1.wireOp",EDGE,"E7.1.0.0");var subQ2=makeQuery(id+"F1.imprint","INTERSECT",VERTEX,{"derivedFrom":[subQ1,subQ0]});Q17=makeQuery(id+"F1.imprint","IMPRINT",FACE,{"disambiguationData":[TD([[makeQuery(id+"F1.imprint","IMPRINT",EDGE,{"disambiguationData":[TD([[subQ2,-1.0]])],"derivedFrom":subQ1}),-1.0]])]});}
            var Q18;
            {var subQ0=sQuery(id+"F1.wireOp",EDGE,"E7.1.0.1");var subQ1=sQuery(id+"F1.wireOp",EDGE,"E4.top");var subQ2=makeQuery(id+"F1.imprint","INTERSECT",VERTEX,{"disambiguationData":[OD(1.0)],"derivedFrom":[subQ1,subQ0]});Q18=makeQuery(id+"F1.imprint","IMPRINT",FACE,{"disambiguationData":[TD([[makeQuery(id+"F1.imprint","IMPRINT",EDGE,{"disambiguationData":[TD([[subQ2,-1.0]])],"derivedFrom":subQ1}),1.0]])]});}
            var Q19;
            {var subQ0=sQuery(id+"F1.wireOp",EDGE,"E8.0");var subQ1=sQuery(id+"F1.wireOp",EDGE,"E7.1.0.0");var subQ2=makeQuery(id+"F1.imprint","INTERSECT",VERTEX,{"derivedFrom":[subQ1,subQ0]});Q19=makeQuery(id+"F1.imprint","IMPRINT",FACE,{"disambiguationData":[TD([[makeQuery(id+"F1.imprint","IMPRINT",EDGE,{"disambiguationData":[TD([[subQ2,-1.0]])],"derivedFrom":subQ1}),1.0]])]});}
            var Q20;
            {var subQ0=sQuery(id+"F1.wireOp",EDGE,"E7.1.0.0");var subQ1=sQuery(id+"F1.wireOp",EDGE,"E4.top");var subQ2=makeQuery(id+"F1.imprint","INTERSECT",VERTEX,{"disambiguationData":[OD(0.0)],"derivedFrom":[subQ1,subQ0]});Q20=makeQuery(id+"F1.imprint","IMPRINT",FACE,{"disambiguationData":[TD([[makeQuery(id+"F1.imprint","IMPRINT",EDGE,{"disambiguationData":[TD([[subQ2,-1.0]])],"derivedFrom":subQ1}),1.0]])]});}
            var Q21;
            {var subQ0=sQuery(id+"F1.wireOp",EDGE,"E7.1.0.0");var subQ1=sQuery(id+"F1.wireOp",EDGE,"E1.top");var subQ2=makeQuery(id+"F1.imprint","INTERSECT",VERTEX,{"disambiguationData":[OD(1.0)],"derivedFrom":[subQ1,subQ0]});Q21=makeQuery(id+"F1.imprint","IMPRINT",FACE,{"disambiguationData":[TD([[makeQuery(id+"F1.imprint","IMPRINT",EDGE,{"disambiguationData":[TD([[subQ2,1.0]])],"derivedFrom":subQ1}),1.0]])]});}
            var Q22;
            {var subQ0=sQuery(id+"F1.wireOp",EDGE,"E7.1.0.0");var subQ1=sQuery(id+"F1.wireOp",EDGE,"E1.top");var subQ2=makeQuery(id+"F1.imprint","INTERSECT",VERTEX,{"disambiguationData":[OD(1.0)],"derivedFrom":[subQ1,subQ0]});Q22=makeQuery(id+"F1.imprint","IMPRINT",FACE,{"disambiguationData":[TD([[makeQuery(id+"F1.imprint","IMPRINT",EDGE,{"disambiguationData":[TD([[subQ2,-1.0]])],"derivedFrom":subQ1}),1.0]])]});}
            var Q23;
            {var subQ0=sQuery(id+"F1.wireOp",EDGE,"E7.1.0.0");var subQ1=sQuery(id+"F1.wireOp",EDGE,"E1.top");var subQ2=makeQuery(id+"F1.imprint","INTERSECT",VERTEX,{"disambiguationData":[OD(0.0)],"derivedFrom":[subQ1,subQ0]});Q23=makeQuery(id+"F1.imprint","IMPRINT",FACE,{"disambiguationData":[TD([[makeQuery(id+"F1.imprint","IMPRINT",EDGE,{"disambiguationData":[TD([[subQ2,-1.0]])],"derivedFrom":subQ1}),1.0]])]});}
            var Q24;
            {var subQ0=sQuery(id+"F1.wireOp",EDGE,"E7.2.0.0");var subQ1=sQuery(id+"F1.wireOp",EDGE,"E1.top");var subQ2=makeQuery(id+"F1.imprint","INTERSECT",VERTEX,{"derivedFrom":[subQ1,subQ0]});Q24=makeQuery(id+"F1.imprint","IMPRINT",FACE,{"disambiguationData":[TD([[makeQuery(id+"F1.imprint","IMPRINT",EDGE,{"disambiguationData":[TD([[subQ2,-1.0]])],"derivedFrom":subQ1}),1.0]])]});}
            var Q25;
            {var subQ0=sQuery(id+"F1.wireOp",EDGE,"E7.2.0.0");var subQ1=sQuery(id+"F1.wireOp",EDGE,"E1.top");var subQ2=makeQuery(id+"F1.imprint","INTERSECT",VERTEX,{"derivedFrom":[subQ1,subQ0]});Q25=makeQuery(id+"F1.imprint","IMPRINT",FACE,{"disambiguationData":[TD([[makeQuery(id+"F1.imprint","IMPRINT",EDGE,{"disambiguationData":[TD([[subQ2,1.0]])],"derivedFrom":subQ1}),1.0]])]});}
            var Q26;
            {var subQ0=sQuery(id+"F1.wireOp",EDGE,"E7.2.0.1");var subQ1=sQuery(id+"F1.wireOp",EDGE,"E4.top");var subQ2=makeQuery(id+"F1.imprint","INTERSECT",VERTEX,{"derivedFrom":[subQ1,subQ0]});Q26=makeQuery(id+"F1.imprint","IMPRINT",FACE,{"disambiguationData":[TD([[makeQuery(id+"F1.imprint","IMPRINT",EDGE,{"disambiguationData":[TD([[subQ2,-1.0]])],"derivedFrom":subQ1}),1.0]])]});}
            var Q27;
            {var subQ0=sQuery(id+"F1.wireOp",EDGE,"E7.2.0.0");var subQ1=sQuery(id+"F1.wireOp",EDGE,"E1.left");var subQ2=makeQuery(id+"F1.imprint","INTERSECT",VERTEX,{"derivedFrom":[subQ1,subQ0]});Q27=makeQuery(id+"F1.imprint","IMPRINT",FACE,{"disambiguationData":[TD([[makeQuery(id+"F1.imprint","IMPRINT",EDGE,{"disambiguationData":[TD([[subQ2,-1.0]])],"derivedFrom":subQ1}),1.0]])]});}
            var Q28;
            {var subQ0=sQuery(id+"F1.wireOp",EDGE,"E7.2.1.0");var subQ1=sQuery(id+"F1.wireOp",EDGE,"E1.left");var subQ2=makeQuery(id+"F1.imprint","INTERSECT",VERTEX,{"disambiguationData":[OD(1.0)],"derivedFrom":[subQ1,subQ0]});Q28=makeQuery(id+"F1.imprint","IMPRINT",FACE,{"disambiguationData":[TD([[makeQuery(id+"F1.imprint","IMPRINT",EDGE,{"disambiguationData":[TD([[subQ2,-1.0]])],"derivedFrom":subQ1}),1.0]])]});}
            var Q29;
            {var subQ0=sQuery(id+"F1.wireOp",EDGE,"E7.2.1.0");var subQ1=sQuery(id+"F1.wireOp",EDGE,"E1.left");var subQ2=makeQuery(id+"F1.imprint","INTERSECT",VERTEX,{"disambiguationData":[OD(1.0)],"derivedFrom":[subQ1,subQ0]});Q29=makeQuery(id+"F1.imprint","IMPRINT",FACE,{"disambiguationData":[TD([[makeQuery(id+"F1.imprint","IMPRINT",EDGE,{"disambiguationData":[TD([[subQ2,1.0]])],"derivedFrom":subQ1}),1.0]])]});}
            var Q30;
            {var subQ0=sQuery(id+"F1.wireOp",EDGE,"E7.2.1.1");var subQ1=sQuery(id+"F1.wireOp",EDGE,"E4.left");var subQ2=makeQuery(id+"F1.imprint","INTERSECT",VERTEX,{"disambiguationData":[OD(1.0)],"derivedFrom":[subQ1,subQ0]});Q30=makeQuery(id+"F1.imprint","IMPRINT",FACE,{"disambiguationData":[TD([[makeQuery(id+"F1.imprint","IMPRINT",EDGE,{"disambiguationData":[TD([[subQ2,-1.0]])],"derivedFrom":subQ1}),1.0]])]});}
            var Q31;
            {var subQ0=sQuery(id+"F1.wireOp",EDGE,"E11.0");var subQ1=sQuery(id+"F1.wireOp",EDGE,"E7.2.1.0");var subQ2=makeQuery(id+"F1.imprint","INTERSECT",VERTEX,{"derivedFrom":[subQ1,subQ0]});Q31=makeQuery(id+"F1.imprint","IMPRINT",FACE,{"disambiguationData":[TD([[makeQuery(id+"F1.imprint","IMPRINT",EDGE,{"disambiguationData":[TD([[subQ2,-1.0]])],"derivedFrom":subQ1}),1.0]])]});}
            var Q32;
            {var subQ0=sQuery(id+"F1.wireOp",EDGE,"E11.0");var subQ1=sQuery(id+"F1.wireOp",EDGE,"E7.1.1.0");var subQ2=makeQuery(id+"F1.imprint","INTERSECT",VERTEX,{"disambiguationData":[OD(0.0)],"derivedFrom":[subQ1,subQ0]});Q32=makeQuery(id+"F1.imprint","IMPRINT",FACE,{"disambiguationData":[TD([[makeQuery(id+"F1.imprint","IMPRINT",EDGE,{"disambiguationData":[TD([[subQ2,1.0]])],"derivedFrom":subQ1}),-1.0]])]});}
            var Q33;
            {var subQ0=sQuery(id+"F1.wireOp",EDGE,"E7.2.1.0");var subQ1=sQuery(id+"F1.wireOp",EDGE,"E4.left");var subQ2=makeQuery(id+"F1.imprint","INTERSECT",VERTEX,{"disambiguationData":[OD(0.0)],"derivedFrom":[subQ1,subQ0]});Q33=makeQuery(id+"F1.imprint","IMPRINT",FACE,{"disambiguationData":[TD([[makeQuery(id+"F1.imprint","IMPRINT",EDGE,{"disambiguationData":[TD([[subQ2,-1.0]])],"derivedFrom":subQ1}),1.0]])]});}
            var Q34;
            {var subQ0=sQuery(id+"F1.wireOp",EDGE,"E7.2.1.0");var subQ1=sQuery(id+"F1.wireOp",EDGE,"E1.left");var subQ2=makeQuery(id+"F1.imprint","INTERSECT",VERTEX,{"disambiguationData":[OD(0.0)],"derivedFrom":[subQ1,subQ0]});Q34=makeQuery(id+"F1.imprint","IMPRINT",FACE,{"disambiguationData":[TD([[makeQuery(id+"F1.imprint","IMPRINT",EDGE,{"disambiguationData":[TD([[subQ2,-1.0]])],"derivedFrom":subQ1}),1.0]])]});}
            var Q35;
            {var subQ0=sQuery(id+"F1.wireOp",EDGE,"E7.2.2.0");var subQ1=sQuery(id+"F1.wireOp",EDGE,"E1.left");var subQ2=makeQuery(id+"F1.imprint","INTERSECT",VERTEX,{"derivedFrom":[subQ1,subQ0]});Q35=makeQuery(id+"F1.imprint","IMPRINT",FACE,{"disambiguationData":[TD([[makeQuery(id+"F1.imprint","IMPRINT",EDGE,{"disambiguationData":[TD([[subQ2,-1.0]])],"derivedFrom":subQ1}),1.0]])]});}
            var Q36;
            {var subQ0=sQuery(id+"F1.wireOp",EDGE,"E7.2.2.0");var subQ1=sQuery(id+"F1.wireOp",EDGE,"E1.left");var subQ2=makeQuery(id+"F1.imprint","INTERSECT",VERTEX,{"derivedFrom":[subQ1,subQ0]});Q36=makeQuery(id+"F1.imprint","IMPRINT",FACE,{"disambiguationData":[TD([[makeQuery(id+"F1.imprint","IMPRINT",EDGE,{"disambiguationData":[TD([[subQ2,1.0]])],"derivedFrom":subQ1}),1.0]])]});}
            var Q37;
            {var subQ0=sQuery(id+"F1.wireOp",EDGE,"E7.2.2.1");var subQ1=sQuery(id+"F1.wireOp",EDGE,"E4.bottom");var subQ2=makeQuery(id+"F1.imprint","INTERSECT",VERTEX,{"derivedFrom":[subQ1,subQ0]});Q37=makeQuery(id+"F1.imprint","IMPRINT",FACE,{"disambiguationData":[TD([[makeQuery(id+"F1.imprint","IMPRINT",EDGE,{"disambiguationData":[TD([[subQ2,-1.0]])],"derivedFrom":subQ1}),-1.0]])]});}
            var Q38;
            {var subQ0=sQuery(id+"F1.wireOp",EDGE,"E7.2.2.0");var subQ1=sQuery(id+"F1.wireOp",EDGE,"E1.bottom");var subQ2=makeQuery(id+"F1.imprint","INTERSECT",VERTEX,{"derivedFrom":[subQ1,subQ0]});Q38=makeQuery(id+"F1.imprint","IMPRINT",FACE,{"disambiguationData":[TD([[makeQuery(id+"F1.imprint","IMPRINT",EDGE,{"disambiguationData":[TD([[subQ2,1.0]])],"derivedFrom":subQ1}),-1.0]])]});}
            var Q39;
            {var subQ0=sQuery(id+"F1.wireOp",EDGE,"E7.2.2.0");var subQ1=sQuery(id+"F1.wireOp",EDGE,"E1.bottom");var subQ2=makeQuery(id+"F1.imprint","INTERSECT",VERTEX,{"derivedFrom":[subQ1,subQ0]});Q39=makeQuery(id+"F1.imprint","IMPRINT",FACE,{"disambiguationData":[TD([[makeQuery(id+"F1.imprint","IMPRINT",EDGE,{"disambiguationData":[TD([[subQ2,-1.0]])],"derivedFrom":subQ1}),-1.0]])]});}
            var Q40;
            {var subQ0=sQuery(id+"F1.wireOp",EDGE,"E7.1.2.0");var subQ1=sQuery(id+"F1.wireOp",EDGE,"E1.bottom");var subQ2=makeQuery(id+"F1.imprint","INTERSECT",VERTEX,{"disambiguationData":[OD(0.0)],"derivedFrom":[subQ1,subQ0]});Q40=makeQuery(id+"F1.imprint","IMPRINT",FACE,{"disambiguationData":[TD([[makeQuery(id+"F1.imprint","IMPRINT",EDGE,{"disambiguationData":[TD([[subQ2,-1.0]])],"derivedFrom":subQ1}),-1.0]])]});}
            var Q41;
            {var subQ0=sQuery(id+"F1.wireOp",EDGE,"E7.1.2.0");var subQ1=sQuery(id+"F1.wireOp",EDGE,"E4.bottom");var subQ2=makeQuery(id+"F1.imprint","INTERSECT",VERTEX,{"disambiguationData":[OD(0.0)],"derivedFrom":[subQ1,subQ0]});Q41=makeQuery(id+"F1.imprint","IMPRINT",FACE,{"disambiguationData":[TD([[makeQuery(id+"F1.imprint","IMPRINT",EDGE,{"disambiguationData":[TD([[subQ2,-1.0]])],"derivedFrom":subQ1}),-1.0]])]});}
            var Q42;
            {var subQ0=sQuery(id+"F1.wireOp",EDGE,"E9.0");var subQ1=sQuery(id+"F1.wireOp",EDGE,"E7.1.2.0");var subQ2=makeQuery(id+"F1.imprint","INTERSECT",VERTEX,{"derivedFrom":[subQ1,subQ0]});Q42=makeQuery(id+"F1.imprint","IMPRINT",FACE,{"disambiguationData":[TD([[makeQuery(id+"F1.imprint","IMPRINT",EDGE,{"disambiguationData":[TD([[subQ2,-1.0]])],"derivedFrom":subQ1}),1.0]])]});}
            var Q43;
            {var subQ0=sQuery(id+"F1.wireOp",EDGE,"E8.0");var subQ1=sQuery(id+"F1.wireOp",EDGE,"E7.1.1.0");var subQ2=makeQuery(id+"F1.imprint","INTERSECT",VERTEX,{"disambiguationData":[OD(1.0)],"derivedFrom":[subQ1,subQ0]});Q43=makeQuery(id+"F1.imprint","IMPRINT",FACE,{"disambiguationData":[TD([[makeQuery(id+"F1.imprint","IMPRINT",EDGE,{"disambiguationData":[TD([[subQ2,-1.0]])],"derivedFrom":subQ1}),-1.0]])]});}
            var Q44;
            {var subQ0=sQuery(id+"F1.wireOp",EDGE,"E7.1.2.1");var subQ1=sQuery(id+"F1.wireOp",EDGE,"E4.bottom");var subQ2=makeQuery(id+"F1.imprint","INTERSECT",VERTEX,{"disambiguationData":[OD(1.0)],"derivedFrom":[subQ1,subQ0]});Q44=makeQuery(id+"F1.imprint","IMPRINT",FACE,{"disambiguationData":[TD([[makeQuery(id+"F1.imprint","IMPRINT",EDGE,{"disambiguationData":[TD([[subQ2,-1.0]])],"derivedFrom":subQ1}),-1.0]])]});}
            var Q45;
            {var subQ0=sQuery(id+"F1.wireOp",EDGE,"E7.1.2.0");var subQ1=sQuery(id+"F1.wireOp",EDGE,"E1.bottom");var subQ2=makeQuery(id+"F1.imprint","INTERSECT",VERTEX,{"disambiguationData":[OD(1.0)],"derivedFrom":[subQ1,subQ0]});Q45=makeQuery(id+"F1.imprint","IMPRINT",FACE,{"disambiguationData":[TD([[makeQuery(id+"F1.imprint","IMPRINT",EDGE,{"disambiguationData":[TD([[subQ2,1.0]])],"derivedFrom":subQ1}),-1.0]])]});}
            var Q46;
            {var subQ0=sQuery(id+"F1.wireOp",EDGE,"E7.1.2.0");var subQ1=sQuery(id+"F1.wireOp",EDGE,"E1.bottom");var subQ2=makeQuery(id+"F1.imprint","INTERSECT",VERTEX,{"disambiguationData":[OD(1.0)],"derivedFrom":[subQ1,subQ0]});Q46=makeQuery(id+"F1.imprint","IMPRINT",FACE,{"disambiguationData":[TD([[makeQuery(id+"F1.imprint","IMPRINT",EDGE,{"disambiguationData":[TD([[subQ2,-1.0]])],"derivedFrom":subQ1}),-1.0]])]});}
            var Q47;
            {var subQ0=sQuery(id+"F1.wireOp",EDGE,"E7.0.2.0");var subQ1=sQuery(id+"F1.wireOp",EDGE,"E4.bottom");var subQ2=makeQuery(id+"F1.imprint","INTERSECT",VERTEX,{"derivedFrom":[subQ1,subQ0]});Q47=makeQuery(id+"F1.imprint","IMPRINT",FACE,{"disambiguationData":[TD([[makeQuery(id+"F1.imprint","IMPRINT",EDGE,{"disambiguationData":[TD([[subQ2,-1.0]])],"derivedFrom":subQ1}),-1.0]])]});}
            var Q48;
            {var subQ0=sQuery(id+"F1.wireOp",EDGE,"E7.0.2.0");var subQ1=sQuery(id+"F1.wireOp",EDGE,"E1.right");var subQ2=makeQuery(id+"F1.imprint","INTERSECT",VERTEX,{"derivedFrom":[subQ1,subQ0]});Q48=makeQuery(id+"F1.imprint","IMPRINT",FACE,{"disambiguationData":[TD([[makeQuery(id+"F1.imprint","IMPRINT",EDGE,{"disambiguationData":[TD([[subQ2,1.0]])],"derivedFrom":subQ1}),-1.0]])]});}
            var Q49;
            {var subQ0=sQuery(id+"F1.wireOp",EDGE,"E7.0.2.0");var subQ1=sQuery(id+"F1.wireOp",EDGE,"E1.right");var subQ2=makeQuery(id+"F1.imprint","INTERSECT",VERTEX,{"derivedFrom":[subQ1,subQ0]});Q49=makeQuery(id+"F1.imprint","IMPRINT",FACE,{"disambiguationData":[TD([[makeQuery(id+"F1.imprint","IMPRINT",EDGE,{"disambiguationData":[TD([[subQ2,-1.0]])],"derivedFrom":subQ1}),-1.0]])]});}
            var Q50;
            {var subQ0=sQuery(id+"F1.wireOp",EDGE,"E7.0.1.0");var subQ1=sQuery(id+"F1.wireOp",EDGE,"E1.right");var subQ2=makeQuery(id+"F1.imprint","INTERSECT",VERTEX,{"disambiguationData":[OD(0.0)],"derivedFrom":[subQ1,subQ0]});Q50=makeQuery(id+"F1.imprint","IMPRINT",FACE,{"disambiguationData":[TD([[makeQuery(id+"F1.imprint","IMPRINT",EDGE,{"disambiguationData":[TD([[subQ2,-1.0]])],"derivedFrom":subQ1}),-1.0]])]});}
            var Q51;
            {var subQ0=sQuery(id+"F1.wireOp",EDGE,"E7.0.2.0");var subQ1=sQuery(id+"F1.wireOp",EDGE,"E1.bottom");var subQ2=makeQuery(id+"F1.imprint","INTERSECT",VERTEX,{"derivedFrom":[subQ1,subQ0]});Q51=makeQuery(id+"F1.imprint","IMPRINT",FACE,{"disambiguationData":[TD([[makeQuery(id+"F1.imprint","IMPRINT",EDGE,{"disambiguationData":[TD([[subQ2,-1.0]])],"derivedFrom":subQ1}),-1.0]])]});}
            extrude(context, id + "F4", {"entities" : qUnion([Q0, Q1, Q2, Q3, Q4, Q5, Q6, Q7, Q8, Q9, Q10, Q11, Q12, Q13, Q14, Q15, Q16, Q17, Q18, Q19, Q20, Q21, Q22, Q23, Q24, Q25, Q26, Q27, Q28, Q29, Q30, Q31, Q32, Q33, Q34, Q35, Q36, Q37, Q38, Q39, Q40, Q41, Q42, Q43, Q44, Q45, Q46, Q47, Q48, Q49, Q50, Q51]), "depth" : 6.35 * mm, "offsetDistance" : 30.48 * mm});
        }
    });
